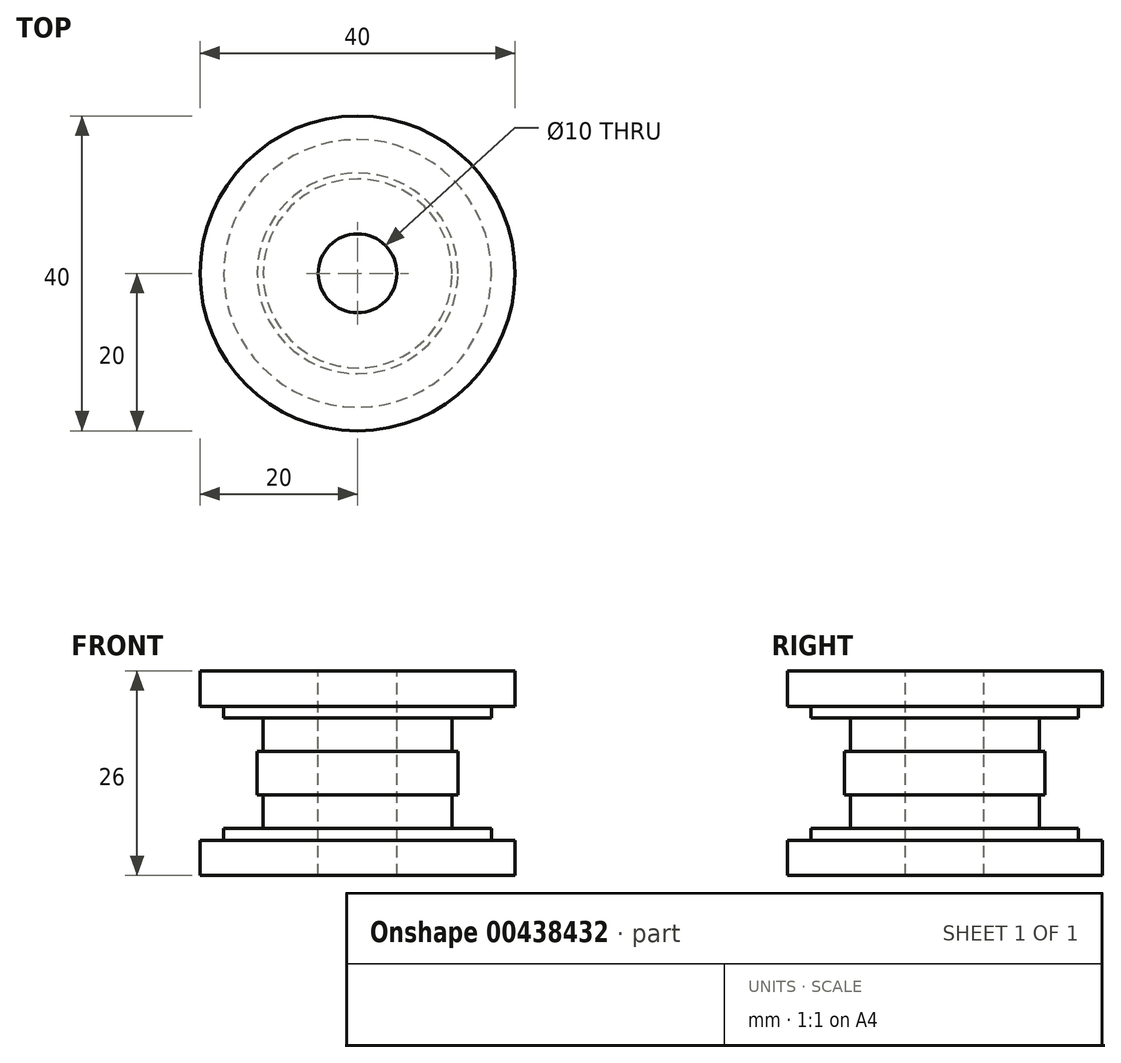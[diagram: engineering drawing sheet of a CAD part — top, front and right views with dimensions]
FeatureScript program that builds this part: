
annotation { "Feature Type Name" : "Feature", "Feature Type Description" : "" }
export const myFeature = defineFeature(function(context is Context, id is Id, definition is map)
    precondition{}
    {
        {
            var Q0;
            Q0=qCreatedBy(makeId("Top.planeOp"),FACE);
            var sketch = newSketch(context, id + "F0", { "sketchPlane" : qUnion([Q0])});
            skCircle(sketch, "E0", {"center": v(0, 0) * mm, "radius": 20 * mm});
            skSolve(sketch);
        }
        {
            var Q0;
            Q0 = qSketchRegion(id + "F0", true);
            extrude(context, id + "F1", {"entities" : qUnion([Q0]), "depth" : 4.5 * mm});
        }
        {
            var Q0;
            Q0=makeQuery(id+"F1.opExtrude","CAP_FACE",FACE,{"disambiguationData":[OSD([sQuery(id+"F0.wireOp",EDGE,"E0")])],"isStart":false});
            var sketch = newSketch(context, id + "F2", { "sketchPlane" : qUnion([Q0])});
            skCircle(sketch, "E1", {"center": v(0, 0) * mm, "radius": 17 * mm});
            skSolve(sketch);
        }
        {
            var Q0;
            Q0 = qSketchRegion(id + "F2", true);
            extrude(context, id + "F3", {"entities" : qUnion([Q0]), "operationType" : NewBodyOperationType.ADD, "depth" : 1.5 * mm});
        }
        {
            var Q0;
            Q0=makeQuery(id+"F3.opExtrude","CAP_FACE",FACE,{"disambiguationData":[OSD([sQuery(id+"F2.wireOp",EDGE,"E1")])],"isStart":false});
            var sketch = newSketch(context, id + "F4", { "sketchPlane" : qUnion([Q0])});
            skCircle(sketch, "E2", {"center": v(0, 0) * mm, "radius": 12 * mm});
            skSolve(sketch);
        }
        {
            var Q0;
            Q0 = qSketchRegion(id + "F4", true);
            extrude(context, id + "F5", {"entities" : qUnion([Q0]), "operationType" : NewBodyOperationType.ADD, "depth" : 4.25 * mm});
        }
        {
            var Q0;
            Q0=makeQuery(id+"F5.opExtrude","CAP_FACE",FACE,{"disambiguationData":[OSD([sQuery(id+"F4.wireOp",EDGE,"E2")])],"isStart":false});
            var sketch = newSketch(context, id + "F6", { "sketchPlane" : qUnion([Q0])});
            skCircle(sketch, "E3", {"center": v(0, 0) * mm, "radius": 12.75 * mm});
            skSolve(sketch);
        }
        {
            var Q0;
            Q0 = qSketchRegion(id + "F6", true);
            extrude(context, id + "F7", {"entities" : qUnion([Q0]), "operationType" : NewBodyOperationType.ADD, "depth" : 5.5 * mm});
        }
        {
            var Q0;
            Q0=makeQuery(id+"F7.opExtrude","CAP_FACE",FACE,{"disambiguationData":[OSD([sQuery(id+"F6.wireOp",EDGE,"E3")])],"isStart":false});
            var sketch = newSketch(context, id + "F8", { "sketchPlane" : qUnion([Q0])});
            skCircle(sketch, "E4", {"center": v(0, 0) * mm, "radius": 12 * mm});
            skSolve(sketch);
        }
        {
            var Q0;
            Q0 = qSketchRegion(id + "F8", true);
            extrude(context, id + "F9", {"entities" : qUnion([Q0]), "operationType" : NewBodyOperationType.ADD, "depth" : 4.25 * mm});
        }
        {
            var Q0;
            Q0=makeQuery(id+"F9.opExtrude","CAP_FACE",FACE,{"disambiguationData":[OSD([sQuery(id+"F8.wireOp",EDGE,"E4")])],"isStart":false});
            var sketch = newSketch(context, id + "F10", { "sketchPlane" : qUnion([Q0])});
            skCircle(sketch, "E5", {"center": v(0, 0) * mm, "radius": 17 * mm});
            skSolve(sketch);
        }
        {
            var Q0;
            Q0 = qSketchRegion(id + "F10", true);
            extrude(context, id + "F11", {"entities" : qUnion([Q0]), "operationType" : NewBodyOperationType.ADD, "depth" : 1.5 * mm});
        }
        {
            var Q0;
            Q0=makeQuery(id+"F11.opExtrude","CAP_FACE",FACE,{"disambiguationData":[OSD([sQuery(id+"F10.wireOp",EDGE,"E5")])],"isStart":false});
            var sketch = newSketch(context, id + "F12", { "sketchPlane" : qUnion([Q0])});
            skCircle(sketch, "E6", {"center": v(0, 0) * mm, "radius": 20 * mm});
            skSolve(sketch);
        }
        {
            var Q0;
            Q0 = qSketchRegion(id + "F12", true);
            extrude(context, id + "F13", {"entities" : qUnion([Q0]), "operationType" : NewBodyOperationType.ADD, "depth" : 4.5 * mm});
        }
        {
            var Q0;
            Q0=makeQuery(id+"F13.opExtrude","CAP_FACE",FACE,{"disambiguationData":[OSD([sQuery(id+"F12.wireOp",EDGE,"E6")])],"isStart":false});
            var sketch = newSketch(context, id + "F14", { "sketchPlane" : qUnion([Q0])});
            skCircle(sketch, "E7", {"center": v(0, 0) * mm, "radius": 5 * mm});
            skSolve(sketch);
        }
        {
            var Q0;
            Q0 = qSketchRegion(id + "F14", true);
            extrude(context, id + "F15", {"entities" : qUnion([Q0]), "operationType" : NewBodyOperationType.REMOVE, "oppositeDirection" : true, "depth" : 30 * mm});
        }
    });
